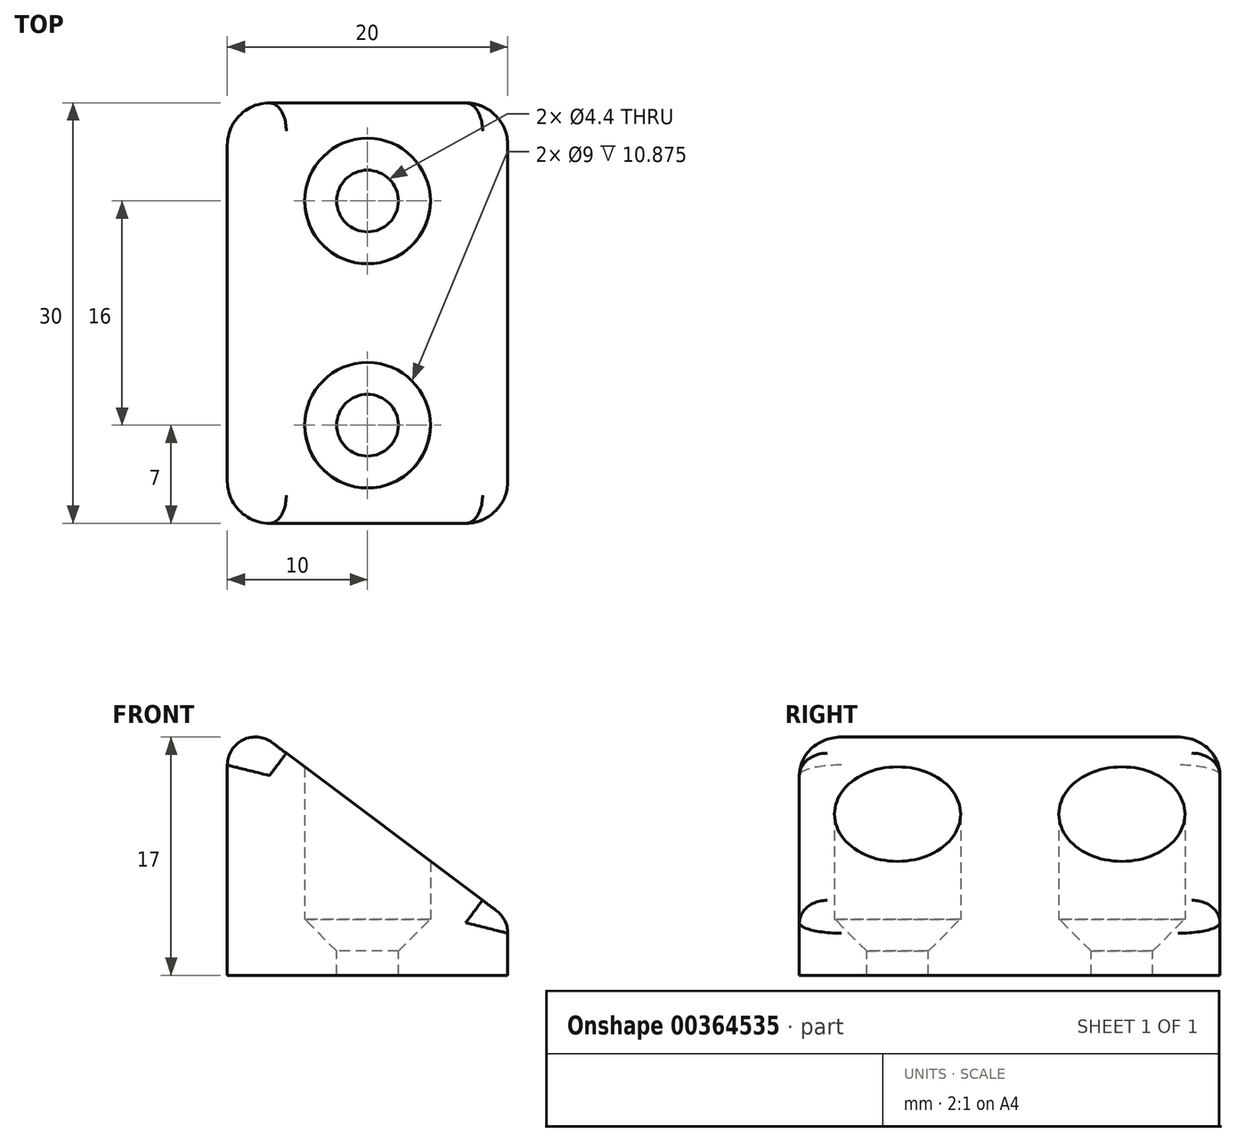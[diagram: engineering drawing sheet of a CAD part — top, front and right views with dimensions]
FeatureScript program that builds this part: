
annotation { "Feature Type Name" : "Feature", "Feature Type Description" : "" }
export const myFeature = defineFeature(function(context is Context, id is Id, definition is map)
    precondition{}
    {
        {
            var Q0;
            Q0=qCreatedBy(makeId("Top.planeOp"),FACE);
            var sketch = newSketch(context, id + "F0", { "sketchPlane" : qUnion([Q0])});
            skLineSegment(sketch, "E0.bottom", {"start": v(0, 0) * mm, "end": v(20, 0) * mm});
            skLineSegment(sketch, "E0.top", {"start": v(0, 30) * mm, "end": v(20, 30) * mm});
            skLineSegment(sketch, "E0.left", {"start": v(0, 0) * mm, "end": v(0, 30) * mm});
            skLineSegment(sketch, "E0.right", {"start": v(20, 0) * mm, "end": v(20, 30) * mm});
            skSolve(sketch);
        }
        {
            var Q0;
            Q0=makeQuery(id+"F0.imprint","IMPRINT",FACE,{"disambiguationData":[TD([[makeQuery(id+"F0.imprint","IMPRINT",EDGE,{"derivedFrom":sQuery(id+"F0.wireOp",EDGE,"E0.bottom")}),1.0]])]});
            extrude(context, id + "F1", {"entities" : qUnion([Q0]), "depth" : 4 * mm});
        }
        {
            var Q0;
            Q0=makeQuery(id+"F1.opExtrude","CAP_FACE",FACE,{"disambiguationData":[OSD([sQuery(id+"F0.wireOp",EDGE,"E0.bottom"),sQuery(id+"F0.wireOp",EDGE,"E0.top"),sQuery(id+"F0.wireOp",EDGE,"E0.left"),sQuery(id+"F0.wireOp",EDGE,"E0.right")])],"isStart":false});
            var sketch = newSketch(context, id + "F2", { "sketchPlane" : qUnion([Q0])});
            skLineSegment(sketch, "E1", {"start": v(10, 30) * mm, "end": v(10, 0) * mm});
            skPoint(sketch, "E2", {"position": v(10, 23) * mm});
            skPoint(sketch, "E3", {"position": v(10, 7) * mm});
            skSolve(sketch);
        }
        {
            var Q0;
            Q0=sQuery(id+"F2.wireOp",VERTEX,"E2");
            var Q1;
            Q1=sQuery(id+"F2.wireOp",VERTEX,"E3");
            var Q2;
            Q2=makeQuery(id+"F1.opExtrude","SWEPT_BODY",BODY,{"disambiguationData":[OSD([sQuery(id+"F0.wireOp",EDGE,"E0.bottom"),sQuery(id+"F0.wireOp",EDGE,"E0.top"),sQuery(id+"F0.wireOp",EDGE,"E0.left"),sQuery(id+"F0.wireOp",EDGE,"E0.right")])]});
            hole(context, id + "F3", {"style" : HoleStyle.C_SINK, "endStyle" : HoleEndStyle.THROUGH, "standardTappedOrClearance" : lookupTablePath({ "standard" : "ISO", "fit" : "Normal", "size" : "M4", "type" : "Clearance" }), "standardBlindInLast" : lookupTablePath({ "fit" : "Standard", "standard" : "ISO", "size" : "M4", "type" : "Clearance" }), "holeDiameter" : 4.4 * mm, "cSinkDiameter" : 8.96 * mm, "cSinkAngle" : 90 * degree, "isTappedThrough" : true, "tappedDepth" : 12 * mm, "tapClearance" : 3, "locations" : qUnion([Q0, Q1]), "scope" : qUnion([Q2])});
        }
        {
            var Q0;
            Q0=makeQuery(id+"F1.opExtrude","SWEPT_FACE",FACE,{"disambiguationData":[OSD([sQuery(id+"F0.wireOp",EDGE,"E0.bottom")])]});
            var sketch = newSketch(context, id + "F4", { "sketchPlane" : qUnion([Q0])});
            skLineSegment(sketch, "E4", {"start": v(0, 4) * mm, "end": v(0, 19) * mm});
            skLineSegment(sketch, "E5", {"start": v(0, 19) * mm, "end": v(20, 4) * mm});
            skSolve(sketch);
        }
        {
            var Q0;
            Q0=makeQuery(id+"F4.imprint","IMPRINT",FACE,{"disambiguationData":[TD([[makeQuery(id+"F4.imprint","IMPRINT",EDGE,{"derivedFrom":sQuery(id+"F4.wireOp",EDGE,"E4")}),-1.0]])]});
            var Q1;
            Q1=makeQuery(id+"F1.opExtrude","SWEPT_FACE",FACE,{"disambiguationData":[OSD([sQuery(id+"F0.wireOp",EDGE,"E0.top")])]});
            extrude(context, id + "F5", {"entities" : qUnion([Q0]), "operationType" : NewBodyOperationType.ADD, "endBound" : BoundingType.UP_TO_SURFACE, "oppositeDirection" : true, "endBoundEntityFace" : qUnion([Q1]), "depth" : 25 * mm});
        }
        {
            var Q0;
            Q0=sQuery(id+"F2.wireOp",VERTEX,"E2");
            var Q1;
            Q1=sQuery(id+"F2.wireOp",VERTEX,"E3");
            var Q2;
            Q2=makeQuery(id+"F1.opExtrude","SWEPT_BODY",BODY,{"disambiguationData":[OSD([sQuery(id+"F0.wireOp",EDGE,"E0.bottom"),sQuery(id+"F0.wireOp",EDGE,"E0.top"),sQuery(id+"F0.wireOp",EDGE,"E0.left"),sQuery(id+"F0.wireOp",EDGE,"E0.right")])]});
            hole(context, id + "F6", {"style" : HoleStyle.SIMPLE, "endStyle" : HoleEndStyle.THROUGH, "oppositeDirection" : true, "holeDiameter" : 9 * mm, "isTappedThrough" : true, "tappedDepth" : 12 * mm, "tapClearance" : 3, "locations" : qUnion([Q0, Q1]), "scope" : qUnion([Q2])});
        }
        {
            var Q0;
            Q0=makeQuery(id+"F5.boolean.opBoolean","MERGE",EDGE,{"derivedFrom":[makeQuery(id+"F1.opExtrude","SWEPT_EDGE",EDGE,{"disambiguationData":[OSD([sQuery(id+"F0.wireOp",EDGE,"E0.bottom"),sQuery(id+"F0.wireOp",EDGE,"E0.left")])]}),makeQuery(id+"F5.opExtrude","CAP_EDGE",EDGE,{"disambiguationData":[OSD([sQuery(id+"F4.wireOp",EDGE,"E4")])],"isStart":true})]});
            var Q1;
            Q1=makeQuery(id+"F1.opExtrude","SWEPT_EDGE",EDGE,{"disambiguationData":[OSD([sQuery(id+"F0.wireOp",EDGE,"E0.bottom"),sQuery(id+"F0.wireOp",EDGE,"E0.right")])]});
            var Q2;
            Q2=makeQuery(id+"F1.opExtrude","SWEPT_EDGE",EDGE,{"disambiguationData":[OSD([sQuery(id+"F0.wireOp",EDGE,"E0.top"),sQuery(id+"F0.wireOp",EDGE,"E0.right")])]});
            var Q3;
            {var subQ0=sQuery(id+"F0.wireOp",EDGE,"E0.top");Q3=makeQuery(id+"F5.boolean.opBoolean","MERGE",EDGE,{"derivedFrom":[makeQuery(id+"F1.opExtrude","SWEPT_EDGE",EDGE,{"disambiguationData":[OSD([subQ0,sQuery(id+"F0.wireOp",EDGE,"E0.left")])]}),makeQuery(id+"F5.opExtrude","TWEAK_EDGE",EDGE,{"derivedFrom":[makeQuery(id+"F1.opExtrude","SWEPT_FACE",FACE,{"disambiguationData":[OSD([subQ0])]}),makeQuery(id+"F4.imprint","IMPRINT",EDGE,{"derivedFrom":sQuery(id+"F4.wireOp",EDGE,"E4")})]})]});}
            fillet(context, id + "F7", {"entities" : qUnion([Q0, Q1, Q2, Q3]), "radius" : 3 * mm, "tangentPropagation" : true, "allowEdgeOverflow" : false});
        }
        {
            var Q0;
            Q0=makeQuery(id+"F5.opExtrude","TWEAK_EDGE",EDGE,{"derivedFrom":[makeQuery(id+"F1.opExtrude","SWEPT_FACE",FACE,{"disambiguationData":[OSD([sQuery(id+"F0.wireOp",EDGE,"E0.top")])]}),makeQuery(id+"F4.imprint","IMPRINT",EDGE,{"derivedFrom":sQuery(id+"F4.wireOp",EDGE,"E5")})]});
            var Q1;
            Q1=makeQuery(id+"F5.opExtrude","SWEPT_EDGE",EDGE,{"disambiguationData":[OSD([sQuery(id+"F4.wireOp",EDGE,"E4"),sQuery(id+"F4.wireOp",EDGE,"E5")])]});
            var Q2;
            {var subQ0=sQuery(id+"F0.wireOp",EDGE,"E0.right");Q2=makeQuery(id+"F5.boolean.opBoolean","MERGE",EDGE,{"derivedFrom":[makeQuery(id+"F1.opExtrude","CAP_EDGE",EDGE,{"disambiguationData":[OSD([subQ0])],"isStart":false}),makeQuery(id+"F5.opExtrude","SWEPT_EDGE",EDGE,{"disambiguationData":[OSD([sQuery(id+"F0.wireOp",EDGE,"E0.bottom"),subQ0,sQuery(id+"F4.wireOp",EDGE,"E5")])]})]});}
            var Q3;
            Q3=makeQuery(id+"F5.opExtrude","CAP_EDGE",EDGE,{"disambiguationData":[OSD([sQuery(id+"F4.wireOp",EDGE,"E5")])],"isStart":true});
            fillet(context, id + "F8", {"entities" : qUnion([Q0, Q1, Q2, Q3]), "radius" : 2 * mm, "tangentPropagation" : true, "allowEdgeOverflow" : false});
        }
    });
